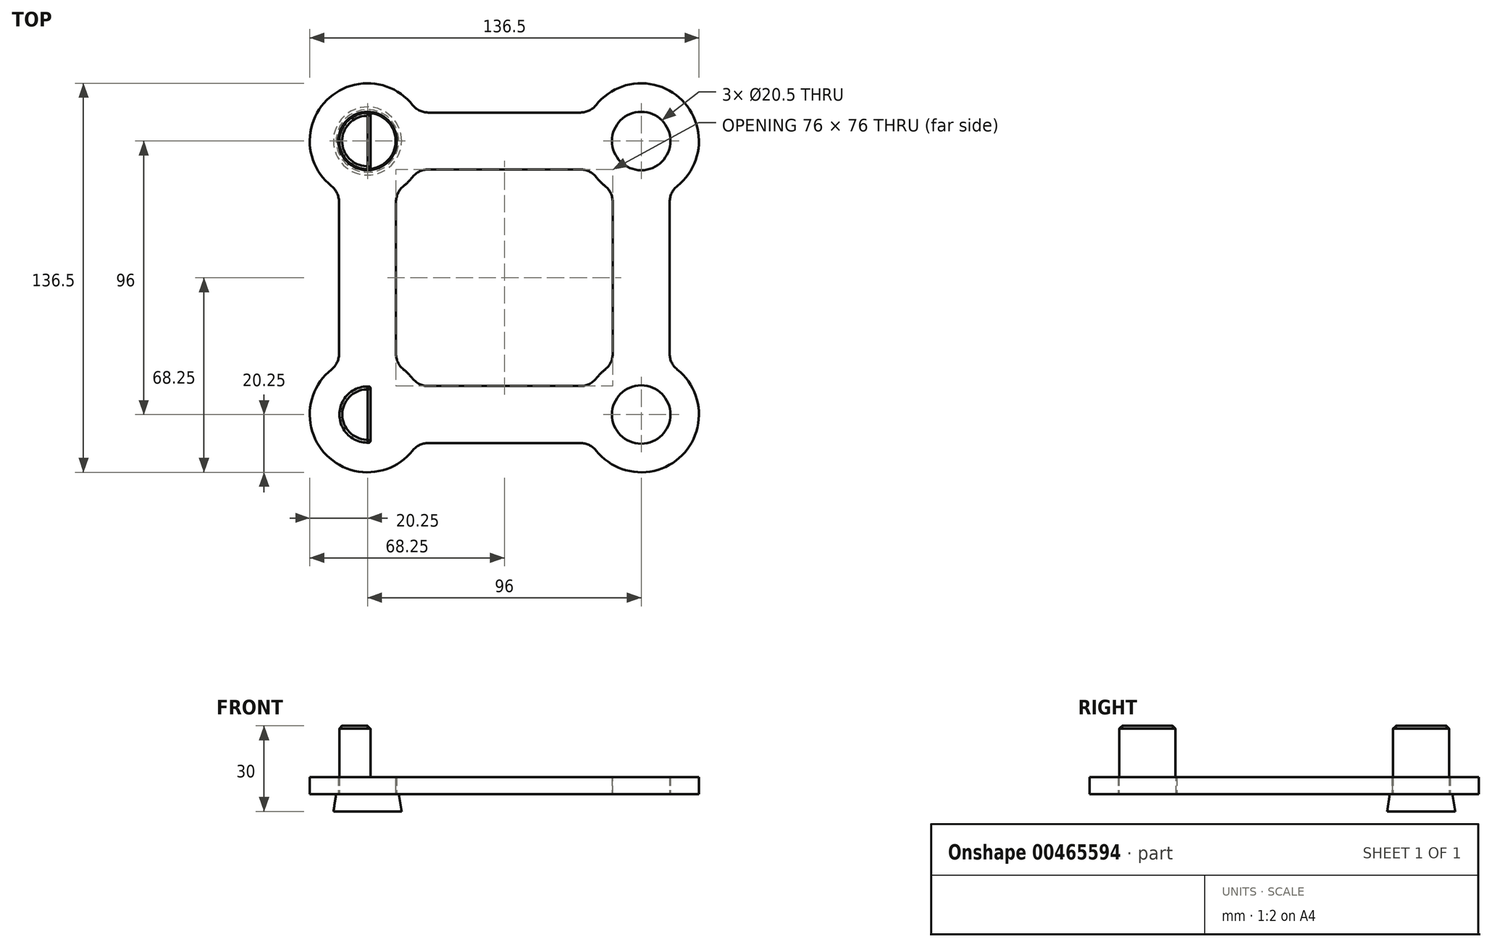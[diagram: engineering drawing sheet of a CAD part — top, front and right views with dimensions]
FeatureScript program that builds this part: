
annotation { "Feature Type Name" : "Feature", "Feature Type Description" : "" }
export const myFeature = defineFeature(function(context is Context, id is Id, definition is map)
    precondition{}
    {
        {
            var Q0;
            Q0=qCreatedBy(makeId("Top.planeOp"),FACE);
            var sketch = newSketch(context, id + "F0", { "sketchPlane" : qUnion([Q0])});
            skCircle(sketch, "E0", {"center": v(0, 0) * mm, "radius": 10.25 * mm, "construction": true});
            skCircle(sketch, "E1.0.1.0", {"center": v(0, 96) * mm, "radius": 10.25 * mm});
            skCircle(sketch, "E1.1.0.0", {"center": v(96, 0) * mm, "radius": 10.25 * mm});
            skCircle(sketch, "E1.1.1.0", {"center": v(96, 96) * mm, "radius": 10.25 * mm});
            skLineSegment(sketch, "E1.direction1", {"start": v(0, 0) * mm, "end": v(96, 0) * mm, "construction": true});
            skLineSegment(sketch, "E1.direction2", {"start": v(0, 0) * mm, "end": v(0, 96) * mm, "construction": true});
            skArc(sketch, "E2.0", {"start": v(-10, 17.6) * mm, "mid": v(-14.32, -14.32) * mm, "end": v(17.6, -10) * mm});
            skLineSegment(sketch, "E3", {"start": v(96, 0) * mm, "end": v(0, 96) * mm, "construction": true});
            skLineSegment(sketch, "E4.trimOffspring", {"start": v(-10, 17.6) * mm, "end": v(-10, 78.4) * mm});
            skLineSegment(sketch, "E5.trimOffspring", {"start": v(10, 17.6) * mm, "end": v(10, 78.4) * mm});
            skArc(sketch, "E6.1.0", {"start": v(78.4, -10) * mm, "mid": v(110.32, -14.32) * mm, "end": v(106, 17.6) * mm});
            skLineSegment(sketch, "E6.1.1", {"start": v(78.4, 10) * mm, "end": v(17.6, 10) * mm});
            skLineSegment(sketch, "E6.1.2", {"start": v(78.4, -10) * mm, "end": v(17.6, -10) * mm});
            skArc(sketch, "E6.2.0", {"start": v(106, 78.4) * mm, "mid": v(110.32, 110.32) * mm, "end": v(78.4, 106) * mm});
            skLineSegment(sketch, "E6.2.1", {"start": v(86, 78.4) * mm, "end": v(86, 17.6) * mm});
            skLineSegment(sketch, "E6.2.2", {"start": v(106, 78.4) * mm, "end": v(106, 17.6) * mm});
            skArc(sketch, "E6.3.0", {"start": v(17.6, 106) * mm, "mid": v(-14.32, 110.32) * mm, "end": v(-10, 78.4) * mm});
            skLineSegment(sketch, "E6.3.1", {"start": v(17.6, 86) * mm, "end": v(78.4, 86) * mm});
            skLineSegment(sketch, "E6.3.2", {"start": v(17.6, 106) * mm, "end": v(78.4, 106) * mm});
            skPoint(sketch, "E6.center", {"position": v(48, 48) * mm});
            skArc(sketch, "E7.trimOffspring", {"start": v(78.4, 86) * mm, "mid": v(81.68, 81.68) * mm, "end": v(86, 78.4) * mm});
            skArc(sketch, "E8.trimOffspring", {"start": v(86, 17.6) * mm, "mid": v(81.68, 14.32) * mm, "end": v(78.4, 10) * mm});
            skArc(sketch, "E9.trimOffspring", {"start": v(17.6, 10) * mm, "mid": v(14.32, 14.32) * mm, "end": v(10, 17.6) * mm});
            skArc(sketch, "E10", {"start": v(10, 78.4) * mm, "mid": v(14.31, 81.69) * mm, "end": v(17.6, 86) * mm});
            skSolve(sketch);
        }
        {
            var Q0;
            Q0=qSketchRegion(id+"F0",true);
            extrude(context, id + "F1", {"entities" : qUnion([Q0]), "depth" : 6 * mm});
        }
        {
            var Q0;
            Q0=makeQuery(id+"F1.opExtrude","CAP_FACE",FACE,{"disambiguationData":[OSD([sQuery(id+"F0.wireOp",EDGE,"E1.0.1.0"),sQuery(id+"F0.wireOp",EDGE,"E1.1.0.0"),sQuery(id+"F0.wireOp",EDGE,"E1.1.1.0"),sQuery(id+"F0.wireOp",EDGE,"E2.0"),sQuery(id+"F0.wireOp",EDGE,"E4.trimOffspring"),sQuery(id+"F0.wireOp",EDGE,"E5.trimOffspring"),sQuery(id+"F0.wireOp",EDGE,"E6.1.0"),sQuery(id+"F0.wireOp",EDGE,"E6.1.1"),sQuery(id+"F0.wireOp",EDGE,"E6.1.2"),sQuery(id+"F0.wireOp",EDGE,"E6.2.0"),sQuery(id+"F0.wireOp",EDGE,"E6.2.1"),sQuery(id+"F0.wireOp",EDGE,"E6.2.2"),sQuery(id+"F0.wireOp",EDGE,"E6.3.0"),sQuery(id+"F0.wireOp",EDGE,"E6.3.1"),sQuery(id+"F0.wireOp",EDGE,"E6.3.2"),sQuery(id+"F0.wireOp",EDGE,"E7.trimOffspring"),sQuery(id+"F0.wireOp",EDGE,"E8.trimOffspring"),sQuery(id+"F0.wireOp",EDGE,"E9.trimOffspring"),sQuery(id+"F0.wireOp",EDGE,"E10")])],"isStart":false});
            var sketch = newSketch(context, id + "F2", { "sketchPlane" : qUnion([Q0])});
            skArc(sketch, "E11", {"start": v(1, 9.8) * mm, "mid": v(-9.85, 0) * mm, "end": v(1, -9.8) * mm});
            skLineSegment(sketch, "E12", {"start": v(1, 9.8) * mm, "end": v(1, -9.8) * mm});
            skSolve(sketch);
        }
        {
            var Q0;
            Q0=qSketchRegion(id+"F2",true);
            extrude(context, id + "F3", {"entities" : qUnion([Q0]), "operationType" : NewBodyOperationType.ADD, "depth" : 18 * mm});
        }
        {
            var Q0;
            Q0=makeQuery(id+"F1.opExtrude","SWEPT_EDGE",EDGE,{"disambiguationData":[OSD([sQuery(id+"F0.wireOp",EDGE,"E5.trimOffspring"),sQuery(id+"F0.wireOp",EDGE,"E10")])]});
            var Q1;
            Q1=makeQuery(id+"F1.opExtrude","SWEPT_EDGE",EDGE,{"disambiguationData":[OSD([sQuery(id+"F0.wireOp",EDGE,"E6.3.1"),sQuery(id+"F0.wireOp",EDGE,"E10")])]});
            var Q2;
            Q2=makeQuery(id+"F1.opExtrude","SWEPT_EDGE",EDGE,{"disambiguationData":[OSD([sQuery(id+"F0.wireOp",EDGE,"E6.2.0"),sQuery(id+"F0.wireOp",EDGE,"E6.2.2")])]});
            var Q3;
            Q3=makeQuery(id+"F1.opExtrude","SWEPT_EDGE",EDGE,{"disambiguationData":[OSD([sQuery(id+"F0.wireOp",EDGE,"E2.0"),sQuery(id+"F0.wireOp",EDGE,"E6.1.2")])]});
            var Q4;
            Q4=makeQuery(id+"F1.opExtrude","SWEPT_EDGE",EDGE,{"disambiguationData":[OSD([sQuery(id+"F0.wireOp",EDGE,"E6.1.0"),sQuery(id+"F0.wireOp",EDGE,"E6.2.2")])]});
            var Q5;
            Q5=makeQuery(id+"F1.opExtrude","SWEPT_EDGE",EDGE,{"disambiguationData":[OSD([sQuery(id+"F0.wireOp",EDGE,"E6.1.1"),sQuery(id+"F0.wireOp",EDGE,"E9.trimOffspring")])]});
            var Q6;
            Q6=makeQuery(id+"F1.opExtrude","SWEPT_EDGE",EDGE,{"disambiguationData":[OSD([sQuery(id+"F0.wireOp",EDGE,"E5.trimOffspring"),sQuery(id+"F0.wireOp",EDGE,"E9.trimOffspring")])]});
            var Q7;
            Q7=makeQuery(id+"F1.opExtrude","SWEPT_EDGE",EDGE,{"disambiguationData":[OSD([sQuery(id+"F0.wireOp",EDGE,"E6.2.0"),sQuery(id+"F0.wireOp",EDGE,"E6.3.2")])]});
            var Q8;
            Q8=makeQuery(id+"F1.opExtrude","SWEPT_EDGE",EDGE,{"disambiguationData":[OSD([sQuery(id+"F0.wireOp",EDGE,"E6.3.0"),sQuery(id+"F0.wireOp",EDGE,"E6.3.2")])]});
            var Q9;
            Q9=makeQuery(id+"F1.opExtrude","SWEPT_EDGE",EDGE,{"disambiguationData":[OSD([sQuery(id+"F0.wireOp",EDGE,"E6.2.1"),sQuery(id+"F0.wireOp",EDGE,"E8.trimOffspring")])]});
            var Q10;
            Q10=makeQuery(id+"F1.opExtrude","SWEPT_EDGE",EDGE,{"disambiguationData":[OSD([sQuery(id+"F0.wireOp",EDGE,"E6.1.1"),sQuery(id+"F0.wireOp",EDGE,"E8.trimOffspring")])]});
            var Q11;
            Q11=makeQuery(id+"F1.opExtrude","SWEPT_EDGE",EDGE,{"disambiguationData":[OSD([sQuery(id+"F0.wireOp",EDGE,"E2.0"),sQuery(id+"F0.wireOp",EDGE,"E4.trimOffspring")])]});
            var Q12;
            Q12=makeQuery(id+"F1.opExtrude","SWEPT_EDGE",EDGE,{"disambiguationData":[OSD([sQuery(id+"F0.wireOp",EDGE,"E4.trimOffspring"),sQuery(id+"F0.wireOp",EDGE,"E6.3.0")])]});
            var Q13;
            Q13=makeQuery(id+"F1.opExtrude","SWEPT_EDGE",EDGE,{"disambiguationData":[OSD([sQuery(id+"F0.wireOp",EDGE,"E6.3.1"),sQuery(id+"F0.wireOp",EDGE,"E7.trimOffspring")])]});
            var Q14;
            Q14=makeQuery(id+"F1.opExtrude","SWEPT_EDGE",EDGE,{"disambiguationData":[OSD([sQuery(id+"F0.wireOp",EDGE,"E6.1.0"),sQuery(id+"F0.wireOp",EDGE,"E6.1.2")])]});
            var Q15;
            Q15=makeQuery(id+"F1.opExtrude","SWEPT_EDGE",EDGE,{"disambiguationData":[OSD([sQuery(id+"F0.wireOp",EDGE,"E6.2.1"),sQuery(id+"F0.wireOp",EDGE,"E7.trimOffspring")])]});
            fillet(context, id + "F4", {"entities" : qUnion([Q0, Q1, Q2, Q3, Q4, Q5, Q6, Q7, Q8, Q9, Q10, Q11, Q12, Q13, Q14, Q15]), "radius" : 7 * mm, "tangentPropagation" : true, "allowEdgeOverflow" : false});
        }
        {
            var Q0;
            Q0=makeQuery(id+"F3.opExtrude","CAP_EDGE",EDGE,{"disambiguationData":[OSD([sQuery(id+"F2.wireOp",EDGE,"E11")])],"isStart":false});
            var Q1;
            Q1=makeQuery(id+"F3.opExtrude","CAP_EDGE",EDGE,{"disambiguationData":[OSD([sQuery(id+"F2.wireOp",EDGE,"E12")])],"isStart":false});
            chamfer(context, id + "F5", {"entities" : qUnion([Q0, Q1]), "width" : 1 * mm, "tangentPropagation" : true});
        }
        {
            var Q0;
            {var subQ0=sQuery(id+"F2.wireOp",EDGE,"E12");var subQ1=sQuery(id+"F2.wireOp",EDGE,"E11");Q0=makeQuery(id+"F3.opExtrude","SWEPT_EDGE",EDGE,{"disambiguationData":[OSD([subQ1,subQ0]),TDD([makeQuery(id+"F2.imprint","INTERSECT",VERTEX,{"disambiguationData":[OD(0.0)],"derivedFrom":[subQ1,subQ0]})])]});}
            var Q1;
            {var subQ0=sQuery(id+"F2.wireOp",EDGE,"E12");var subQ1=sQuery(id+"F2.wireOp",EDGE,"E11");Q1=makeQuery(id+"F3.opExtrude","SWEPT_EDGE",EDGE,{"disambiguationData":[OSD([subQ1,subQ0]),TDD([makeQuery(id+"F2.imprint","INTERSECT",VERTEX,{"disambiguationData":[OD(1.0)],"derivedFrom":[subQ1,subQ0]})])]});}
            var Q2;
            Q2=makeQuery(id+"F5.opChamfer","BLEND_EDGE",EDGE,{"disambiguationData":[OD(1.0)],"blendedFrom":[makeQuery(id+"F3.opExtrude","CAP_EDGE",EDGE,{"disambiguationData":[OSD([sQuery(id+"F2.wireOp",EDGE,"E11")])],"isStart":false}),makeQuery(id+"F3.opExtrude","CAP_EDGE",EDGE,{"disambiguationData":[OSD([sQuery(id+"F2.wireOp",EDGE,"E12")])],"isStart":false})],"blendedInto":[]});
            var Q3;
            Q3=makeQuery(id+"F5.opChamfer","BLEND_EDGE",EDGE,{"disambiguationData":[OD(0.0)],"blendedFrom":[makeQuery(id+"F3.opExtrude","CAP_EDGE",EDGE,{"disambiguationData":[OSD([sQuery(id+"F2.wireOp",EDGE,"E11")])],"isStart":false}),makeQuery(id+"F3.opExtrude","CAP_EDGE",EDGE,{"disambiguationData":[OSD([sQuery(id+"F2.wireOp",EDGE,"E12")])],"isStart":false})],"blendedInto":[]});
            fillet(context, id + "F6", {"entities" : qUnion([Q0, Q1, Q2, Q3]), "radius" : 0.5 * mm, "tangentPropagation" : true, "allowEdgeOverflow" : false});
        }
        {
            var Q0;
            Q0=makeQuery(id+"F1.opExtrude","CAP_FACE",FACE,{"disambiguationData":[OSD([sQuery(id+"F0.wireOp",EDGE,"E1.0.1.0"),sQuery(id+"F0.wireOp",EDGE,"E1.1.0.0"),sQuery(id+"F0.wireOp",EDGE,"E1.1.1.0"),sQuery(id+"F0.wireOp",EDGE,"E2.0"),sQuery(id+"F0.wireOp",EDGE,"E4.trimOffspring"),sQuery(id+"F0.wireOp",EDGE,"E5.trimOffspring"),sQuery(id+"F0.wireOp",EDGE,"E6.1.0"),sQuery(id+"F0.wireOp",EDGE,"E6.1.1"),sQuery(id+"F0.wireOp",EDGE,"E6.1.2"),sQuery(id+"F0.wireOp",EDGE,"E6.2.0"),sQuery(id+"F0.wireOp",EDGE,"E6.2.1"),sQuery(id+"F0.wireOp",EDGE,"E6.2.2"),sQuery(id+"F0.wireOp",EDGE,"E6.3.0"),sQuery(id+"F0.wireOp",EDGE,"E6.3.1"),sQuery(id+"F0.wireOp",EDGE,"E6.3.2"),sQuery(id+"F0.wireOp",EDGE,"E7.trimOffspring"),sQuery(id+"F0.wireOp",EDGE,"E8.trimOffspring"),sQuery(id+"F0.wireOp",EDGE,"E9.trimOffspring"),sQuery(id+"F0.wireOp",EDGE,"E10")])],"isStart":true});
            var sketch = newSketch(context, id + "F7", { "sketchPlane" : qUnion([Q0])});
            skCircle(sketch, "E13", {"center": v(0, -96) * mm, "radius": 11 * mm});
            skSolve(sketch);
        }
        {
            var Q0;
            Q0=qSketchRegion(id+"F7",true);
            extrude(context, id + "F8", {"entities" : qUnion([Q0]), "depth" : 6 * mm, "hasDraft" : true, "draftAngle" : 9 * degree});
        }
        {
            var Q0;
            Q0=makeQuery(id+"F8.opExtrude","CAP_FACE",FACE,{"disambiguationData":[OSD([sQuery(id+"F7.wireOp",EDGE,"E13")])],"isStart":true});
            var sketch = newSketch(context, id + "F9", { "sketchPlane" : qUnion([Q0])});
            skCircle(sketch, "E14", {"center": v(0, 96) * mm, "radius": 9.85 * mm});
            skSolve(sketch);
        }
        {
            var Q0;
            Q0=qSketchRegion(id+"F9",true);
            extrude(context, id + "F10", {"entities" : qUnion([Q0]), "operationType" : NewBodyOperationType.ADD, "depth" : 6 * mm});
        }
        {
            var Q0;
            Q0=makeQuery(id+"F10.opExtrude","CAP_FACE",FACE,{"disambiguationData":[OSD([sQuery(id+"F9.wireOp",EDGE,"E14")])],"isStart":false});
            var sketch = newSketch(context, id + "F11", { "sketchPlane" : qUnion([Q0])});
            skLineSegment(sketch, "E15", {"start": v(1, 105.8) * mm, "end": v(1, 86.2) * mm});
            skArc(sketch, "E16", {"start": v(1, 105.8) * mm, "mid": v(-9.92, 96) * mm, "end": v(1, 86.2) * mm});
            skSolve(sketch);
        }
        {
            var Q0;
            Q0=qSketchRegion(id+"F11",true);
            extrude(context, id + "F12", {"entities" : qUnion([Q0]), "operationType" : NewBodyOperationType.ADD, "depth" : 18 * mm});
        }
        {
            var Q0;
            Q0=makeQuery(id+"F12.opExtrude","CAP_EDGE",EDGE,{"disambiguationData":[OSD([sQuery(id+"F11.wireOp",EDGE,"E16")])],"isStart":false});
            var Q1;
            Q1=makeQuery(id+"F12.opExtrude","CAP_EDGE",EDGE,{"disambiguationData":[OSD([sQuery(id+"F11.wireOp",EDGE,"E15")])],"isStart":false});
            chamfer(context, id + "F13", {"entities" : qUnion([Q0, Q1]), "width" : 1 * mm, "tangentPropagation" : true});
        }
        {
            var Q0;
            {var subQ0=sQuery(id+"F11.wireOp",EDGE,"E16");var subQ1=sQuery(id+"F11.wireOp",EDGE,"E15");var subQ2=sQuery(id+"F9.wireOp",EDGE,"E14");Q0=makeQuery(id+"F12.boolean.opBoolean","SPLIT",EDGE,{"disambiguationData":[TD([makeQuery(id+"F12.opExtrude","CAP_FACE",FACE,{"disambiguationData":[OSD([subQ1,subQ0])],"isStart":false})])],"derivedFrom":makeQuery(id+"F12.opExtrude","SWEPT_EDGE",EDGE,{"disambiguationData":[OSD([subQ2,subQ1,subQ0]),TDD([makeQuery(id+"F11.imprint","INTERSECT",VERTEX,{"disambiguationData":[OD(1.0)],"derivedFrom":[makeQuery(id+"F10.opExtrude","CAP_EDGE",EDGE,{"disambiguationData":[OSD([subQ2])],"isStart":true}),subQ1,subQ0]})])]})});}
            var Q1;
            {var subQ0=sQuery(id+"F11.wireOp",EDGE,"E16");var subQ1=sQuery(id+"F11.wireOp",EDGE,"E15");var subQ2=sQuery(id+"F9.wireOp",EDGE,"E14");Q1=makeQuery(id+"F12.boolean.opBoolean","SPLIT",EDGE,{"disambiguationData":[TD([makeQuery(id+"F12.opExtrude","CAP_FACE",FACE,{"disambiguationData":[OSD([subQ1,subQ0])],"isStart":false})])],"derivedFrom":makeQuery(id+"F12.opExtrude","SWEPT_EDGE",EDGE,{"disambiguationData":[OSD([subQ2,subQ1,subQ0]),TDD([makeQuery(id+"F11.imprint","INTERSECT",VERTEX,{"disambiguationData":[OD(0.0)],"derivedFrom":[makeQuery(id+"F10.opExtrude","CAP_EDGE",EDGE,{"disambiguationData":[OSD([subQ2])],"isStart":true}),subQ1,subQ0]})])]})});}
            var Q2;
            Q2=makeQuery(id+"F13.opChamfer","BLEND_EDGE",EDGE,{"disambiguationData":[OD(1.0)],"blendedFrom":[makeQuery(id+"F12.opExtrude","CAP_EDGE",EDGE,{"disambiguationData":[OSD([sQuery(id+"F11.wireOp",EDGE,"E15")])],"isStart":false}),makeQuery(id+"F12.opExtrude","CAP_EDGE",EDGE,{"disambiguationData":[OSD([sQuery(id+"F11.wireOp",EDGE,"E16")])],"isStart":false})],"blendedInto":[]});
            var Q3;
            Q3=makeQuery(id+"F13.opChamfer","BLEND_EDGE",EDGE,{"disambiguationData":[OD(0.0)],"blendedFrom":[makeQuery(id+"F12.opExtrude","CAP_EDGE",EDGE,{"disambiguationData":[OSD([sQuery(id+"F11.wireOp",EDGE,"E15")])],"isStart":false}),makeQuery(id+"F12.opExtrude","CAP_EDGE",EDGE,{"disambiguationData":[OSD([sQuery(id+"F11.wireOp",EDGE,"E16")])],"isStart":false})],"blendedInto":[]});
            fillet(context, id + "F14", {"entities" : qUnion([Q0, Q1, Q2, Q3]), "radius" : 0.5 * mm, "tangentPropagation" : true, "allowEdgeOverflow" : false});
        }
    });
